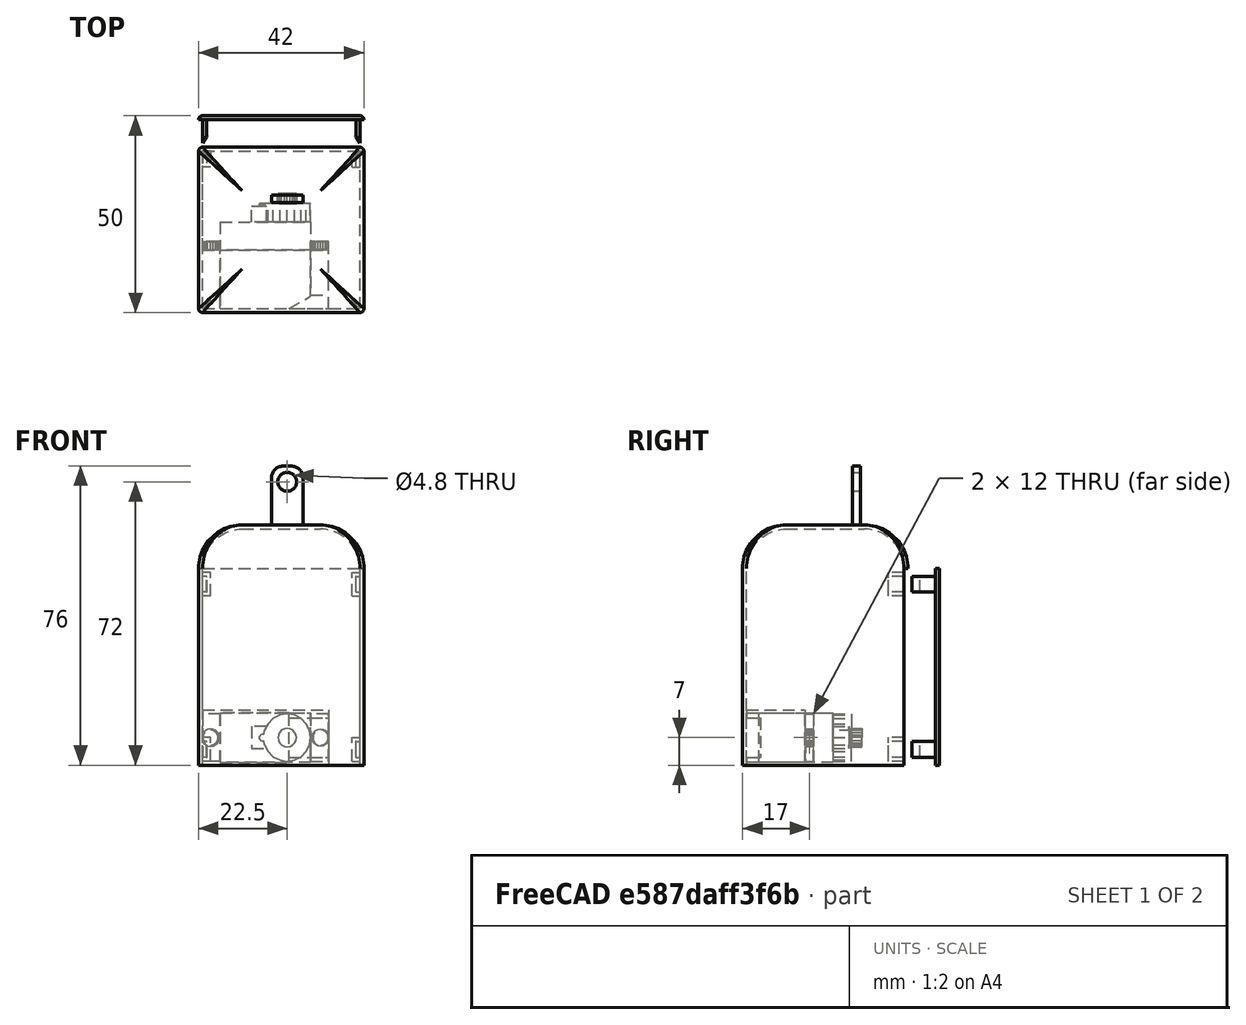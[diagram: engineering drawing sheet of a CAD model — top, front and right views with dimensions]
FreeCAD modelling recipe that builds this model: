
FCSTD DOCUMENT  (FreeCAD 0.21R33771 (Git))
Label: leg draft
License: All rights reserved
LicenseURL: https://en.wikipedia.org/wiki/All_rights_reserved
objects: Part::Box×30, Part::Cut×15, Part::MultiFuse×12, Part::Cylinder×6, Part::Feature×6, Part::Fillet×4, Part::Mirroring×4, App::LinkGroup×2, Part::Thickness×2, Part::MultiCommon×1
note: 80 computed .brp shape members not serialized (recipe doc carries the construction recipe); baked Part::Feature solids carry a one-line shape summary decoded from their .brp

FEATURE [Part::Box] Box  label="leg down"
  AttacherType = Attacher::AttachEngine3D
  Height = 60
  Length = 40
  Placement = pos=(0,0,25) rot=(0,0,1;0rad)
  Width = 40
FEATURE [Part::Box] Box017  label="Cube005"
  AttacherType = Attacher::AttachEngine3D
  Height = 14.9
  Length = 32
  Width = 14
FEATURE [Part::Box] Box018  label="Cube006"
  AttacherType = Attacher::AttachEngine3D
  Height = 3.5
  Length = 10
  Placement = pos=(22,2,0) rot=(0,0,1;0rad)
  Width = 10
FEATURE [Part::Cylinder] Cylinder004  label="Cylindre004"
  Angle = 360
  AttacherType = Attacher::AttachEngine3D
  FirstAngle = 0
  Height = 2.1
  Placement = pos=(2,7,14.9) rot=(0,0,1;0rad)
  Radius = 1.95
  SecondAngle = 0
FEATURE [Part::Cylinder] Cylinder005  label="Cylindre005"
  Angle = 360
  AttacherType = Attacher::AttachEngine3D
  FirstAngle = 0
  Height = 2.1
  Placement = pos=(30,7,14.9) rot=(0,0,1;0rad)
  Radius = 1.95
  SecondAngle = 0
FEATURE [Part::Feature] _g_servo002_solid003  label="9g_servo003"
  Placement = pos=(16,7,11) rot=(0,0,1;0rad)
  shape: bbox 32 x 12.5 x 29.27 mm, 117 faces (baked)
FEATURE [Part::Cut] Cut003
  Base = -> Box017
  Tool = -> _g_servo002_solid003
FEATURE [Part::MultiFuse] Fusion008
  Shapes = -> [Cut003,Cylinder004,Cylinder005]
FEATURE [Part::Cut] Cut004  label="ServoSocket001"
  Base = -> Fusion008
  Placement = pos=(0,0,39) rot=(-1,0,0;1.5708rad)
  Tool = -> Box018
FEATURE [Part::Feature] _g_servo002_solid  label="9g_servo"
  Placement = pos=(16,11,32) rot=(-1,0,0;1.5708rad)
  shape: bbox 32 x 29.27 x 12.5 mm, 117 faces (baked)
FEATURE [Part::Feature] _g_servo_arm_single001
  Placement = pos=(158,31,139) rot=(0,0.707107,-0.707107;3.14159rad)
  shape: bbox 6.653 x 4.702 x 19.83 mm, 2412 faces, 0 solids (baked)
FEATURE [App::LinkGroup] LinkGroup  label="Servo in"
  ElementList = -> [_g_servo002_solid,_g_servo_arm_single001]
  LinkMode = 0
FEATURE [Part::Feature] _g_servo002_solid006  label="9g_servo006"
  Placement = pos=(16,11,32) rot=(-1,0,0;1.5708rad)
  shape: bbox 32 x 29.27 x 12.5 mm, 117 faces (baked)
FEATURE [Part::Feature] _g_servo_arm_single002
  Placement = pos=(158,31,139) rot=(0,0.707107,-0.707107;3.14159rad)
  shape: bbox 6.653 x 4.702 x 19.83 mm, 2412 faces, 0 solids (baked)
FEATURE [App::LinkGroup] LinkGroup001  label="servo up"
  ElementList = -> [_g_servo002_solid006,_g_servo_arm_single002]
  LinkMode = 0
  Placement = pos=(0,-7.62939e-06,65) rot=(0,0,1;0rad)
FEATURE [Part::Box] Box024  label="azeazeaze"
  AttacherType = Attacher::AttachEngine3D
  Height = 15
  Length = 8
  Width = 2
FEATURE [Part::Cylinder] Cylinder010  label="Cylindre010"
  Angle = 360
  AttacherType = Attacher::AttachEngine3D
  FirstAngle = 0
  Height = 10
  Placement = pos=(4,4,11) rot=(1,0,0;1.5708rad)
  Radius = 2.4
  SecondAngle = 0
FEATURE [Part::Cut] Cut
  Base = -> Box024
  Placement = pos=(17.5,26.9,86) rot=(0,0,1;0rad)
  Tool = -> Cylinder010
FEATURE [Part::Fillet] Fillet
  Base = -> Box
  Edges = 4 edges r=10: [Edge2,Edge6,Edge10,Edge12]
FEATURE [Part::Thickness] Thickness
  Faces = -> Fillet [Face4]
  Intersection = true
  Join = 0
  Mode = 0
  SelfIntersection = true
  Value = 1
FEATURE [Part::Fillet] Fillet001
  Base = -> Cut
  Edges = 2 edges r=3: [Edge2,Edge10]
FEATURE [Part::MultiFuse] Fusion
  Shapes = -> [Thickness,Fillet001]
FEATURE [Part::MultiFuse] Fusion011
  Shapes = -> [Fusion,Cut004]
FEATURE [Part::Box] Box025  label="Cube"
  AttacherType = Attacher::AttachEngine3D
  Height = 50
  Length = 42
  Placement = pos=(-1,40,25) rot=(0,0,1;0rad)
  Width = 1
FEATURE [Part::Box] Box026  label="leg down002"
  AttacherType = Attacher::AttachEngine3D
  Height = 60
  Length = 40
  Placement = pos=(0,0,25) rot=(0,0,1;0rad)
  Width = 40
FEATURE [Part::Box] Box027  label="Cube011"
  AttacherType = Attacher::AttachEngine3D
  Height = 14.9
  Length = 32
  Width = 14
FEATURE [Part::Box] Box028  label="Cube012"
  AttacherType = Attacher::AttachEngine3D
  Height = 3.5
  Length = 10
  Placement = pos=(22,2,0) rot=(0,0,1;0rad)
  Width = 10
FEATURE [Part::Box] Box029  label="azeazeaze001"
  AttacherType = Attacher::AttachEngine3D
  Height = 15
  Length = 8
  Width = 2
FEATURE [Part::Cylinder] Cylinder011  label="Cylindre011"
  Angle = 360
  AttacherType = Attacher::AttachEngine3D
  FirstAngle = 0
  Height = 2.1
  Placement = pos=(2,7,14.9) rot=(0,0,1;0rad)
  Radius = 1.95
  SecondAngle = 0
FEATURE [Part::Cylinder] Cylinder012  label="Cylindre012"
  Angle = 360
  AttacherType = Attacher::AttachEngine3D
  FirstAngle = 0
  Height = 2.1
  Placement = pos=(30,7,14.9) rot=(0,0,1;0rad)
  Radius = 1.95
  SecondAngle = 0
FEATURE [Part::Cylinder] Cylinder013  label="Cylindre013"
  Angle = 360
  AttacherType = Attacher::AttachEngine3D
  FirstAngle = 0
  Height = 10
  Placement = pos=(4,4,11) rot=(1,0,0;1.5708rad)
  Radius = 2.4
  SecondAngle = 0
FEATURE [Part::Cut] Cut009
  Base = -> Box029
  Placement = pos=(17.5,26.9,86) rot=(0,0,1;0rad)
  Tool = -> Cylinder013
FEATURE [Part::Fillet] Fillet002
  Base = -> Box026
  Edges = 4 edges r=10: [Edge2,Edge6,Edge10,Edge12]
FEATURE [Part::Fillet] Fillet003
  Base = -> Cut009
  Edges = 2 edges r=3: [Edge2,Edge10]
FEATURE [Part::Thickness] Thickness006
  Faces = -> Fillet002 [Face4]
  Intersection = true
  Join = 0
  Mode = 0
  SelfIntersection = true
  Value = 1
FEATURE [Part::MultiFuse] Fusion012
  Shapes = -> [Thickness006,Fillet003]
FEATURE [Part::Feature] _g_servo002_solid007  label="9g_servo007"
  Placement = pos=(16,7,11) rot=(0,0,1;0rad)
  shape: bbox 32 x 12.5 x 29.27 mm, 117 faces (baked)
FEATURE [Part::Cut] Cut010
  Base = -> Box027
  Tool = -> _g_servo002_solid007
FEATURE [Part::MultiFuse] Fusion013
  Shapes = -> [Cut010,Cylinder011,Cylinder012]
FEATURE [Part::Cut] Cut011  label="ServoSocket004"
  Base = -> Fusion013
  Placement = pos=(0,0,39) rot=(-1,0,0;1.5708rad)
  Tool = -> Box028
FEATURE [Part::MultiFuse] Fusion014
  Shapes = -> [Fusion012,Cut011]
FEATURE [Part::Box] Box030  label="Cube013"
  AttacherType = Attacher::AttachEngine3D
  Height = 50
  Length = 42
  Placement = pos=(-1,40,25) rot=(0,0,1;0rad)
  Width = 1
FEATURE [Part::MultiCommon] Common  label="Leg side"
  Placement = pos=(0,6,0) rot=(0,0,1;0rad)
  Shapes = -> [Fusion014,Box030]
FEATURE [Part::Cut] Cut012  label="Leg body"
  Base = -> Fusion011
  Tool = -> Box025
FEATURE [Part::Box] Box031  label="Cube014"
  AttacherType = Attacher::AttachEngine3D
  Height = 6
  Length = 2
  Width = 4
FEATURE [Part::Box] Box032  label="Cube015"
  AttacherType = Attacher::AttachEngine3D
  Height = 4
  Length = 1
  Placement = pos=(1,0,1) rot=(0,0,1;0rad)
  Width = 4
FEATURE [Part::Box] Box033  label="Cube016"
  AttacherType = Attacher::AttachEngine3D
  Height = 4
  Length = 2
  Placement = pos=(1,0,1) rot=(0,0,-1;0.523599rad)
  Width = 3
FEATURE [Part::Cut] Cut013
  Base = -> Box031
  Placement = pos=(38,36,26) rot=(0,0,1;0rad)
  Tool = -> Box032
FEATURE [Part::Box] Box034  label="Cube017"
  AttacherType = Attacher::AttachEngine3D
  Height = 4
  Length = 1
  Placement = pos=(1,0,1) rot=(0,0,1;0rad)
  Width = 6
FEATURE [Part::Box] Box035  label="Cube018"
  AttacherType = Attacher::AttachEngine3D
  Height = 4
  Length = 1.2
  Placement = pos=(1,0,1) rot=(0,0,1;0rad)
  Width = 2
FEATURE [Part::MultiFuse] Fusion015
  Shapes = -> [Box034,Box035]
FEATURE [Part::Cut] Cut014
  Base = -> Fusion015
  Tool = -> Box033
FEATURE [Part::Mirroring] Part__Mirroring  label="Cut014 (Mirror #1)"
  Base = (0,0,0)
  Normal = (1,0,0)
  Placement = pos=(41,40,26) rot=(0,0,1;0rad)
  Source = -> Cut014
FEATURE [Part::Box] Box036  label="Cube019"
  AttacherType = Attacher::AttachEngine3D
  Height = 6
  Length = 2
  Width = 4
FEATURE [Part::Box] Box037  label="Cube020"
  AttacherType = Attacher::AttachEngine3D
  Height = 4
  Length = 1
  Placement = pos=(1,0,1) rot=(0,0,1;0rad)
  Width = 4
FEATURE [Part::Cut] Cut015
  Base = -> Box036
  Placement = pos=(38,36,68) rot=(0,0,1;0rad)
  Tool = -> Box037
FEATURE [Part::Box] Box038  label="Cube021"
  AttacherType = Attacher::AttachEngine3D
  Height = 4
  Length = 2
  Placement = pos=(1,0,1) rot=(0,0,-1;0.523599rad)
  Width = 3
FEATURE [Part::Box] Box039  label="Cube022"
  AttacherType = Attacher::AttachEngine3D
  Height = 4
  Length = 1
  Placement = pos=(1,0,1) rot=(0,0,1;0rad)
  Width = 6
FEATURE [Part::Box] Box040  label="Cube023"
  AttacherType = Attacher::AttachEngine3D
  Height = 4
  Length = 1.2
  Placement = pos=(1,0,1) rot=(0,0,1;0rad)
  Width = 2
FEATURE [Part::MultiFuse] Fusion016
  Shapes = -> [Box039,Box040]
FEATURE [Part::Cut] Cut016
  Base = -> Fusion016
  Tool = -> Box038
FEATURE [Part::Mirroring] Part__Mirroring001  label="Cut014 (Mirror #1)001"
  Base = (0,0,0)
  Normal = (1,0,0)
  Placement = pos=(41,40,68) rot=(0,0,1;0rad)
  Source = -> Cut016
FEATURE [Part::Box] Box043  label="Cube026"
  AttacherType = Attacher::AttachEngine3D
  Height = 6
  Length = 2
  Width = 4
FEATURE [Part::Box] Box044  label="Cube027"
  AttacherType = Attacher::AttachEngine3D
  Height = 4
  Length = 1
  Placement = pos=(1,0,1) rot=(0,0,1;0rad)
  Width = 4
FEATURE [Part::Cut] Cut018
  Base = -> Box043
  Placement = pos=(2,40,26) rot=(0,0,1;3.14159rad)
  Tool = -> Box044
FEATURE [Part::Box] Box045  label="Cube028"
  AttacherType = Attacher::AttachEngine3D
  Height = 6
  Length = 2
  Width = 4
FEATURE [Part::Box] Box046  label="Cube029"
  AttacherType = Attacher::AttachEngine3D
  Height = 4
  Length = 1
  Placement = pos=(1,0,1) rot=(0,0,1;0rad)
  Width = 4
FEATURE [Part::Cut] Cut019
  Base = -> Box045
  Placement = pos=(2,40,68) rot=(0,0,1;3.14159rad)
  Tool = -> Box046
FEATURE [Part::Box] Box047  label="Cube030"
  AttacherType = Attacher::AttachEngine3D
  Height = 4
  Length = 2
  Placement = pos=(1,0,1) rot=(0,0,-1;0.523599rad)
  Width = 3
FEATURE [Part::Box] Box048  label="Cube031"
  AttacherType = Attacher::AttachEngine3D
  Height = 4
  Length = 1
  Placement = pos=(1,0,1) rot=(0,0,1;0rad)
  Width = 6
FEATURE [Part::Box] Box049  label="Cube032"
  AttacherType = Attacher::AttachEngine3D
  Height = 4
  Length = 1.2
  Placement = pos=(1,0,1) rot=(0,0,1;0rad)
  Width = 2
FEATURE [Part::MultiFuse] Fusion017
  Shapes = -> [Box048,Box049]
FEATURE [Part::Cut] Cut020
  Base = -> Fusion017
  Tool = -> Box047
FEATURE [Part::Mirroring] Part__Mirroring002  label="Cut014 (Mirror #1)002"
  Base = (0,0,0)
  Normal = (1,0,0)
  Placement = pos=(-1,40,32) rot=(0,1,0;3.14159rad)
  Source = -> Cut020
FEATURE [Part::Box] Box050  label="Cube033"
  AttacherType = Attacher::AttachEngine3D
  Height = 4
  Length = 2
  Placement = pos=(1,0,1) rot=(0,0,-1;0.523599rad)
  Width = 3
FEATURE [Part::Box] Box051  label="Cube034"
  AttacherType = Attacher::AttachEngine3D
  Height = 4
  Length = 1
  Placement = pos=(1,0,1) rot=(0,0,1;0rad)
  Width = 6
FEATURE [Part::Box] Box052  label="Cube035"
  AttacherType = Attacher::AttachEngine3D
  Height = 4
  Length = 1.2
  Placement = pos=(1,0,1) rot=(0,0,1;0rad)
  Width = 2
FEATURE [Part::MultiFuse] Fusion018
  Shapes = -> [Box051,Box052]
FEATURE [Part::Cut] Cut021
  Base = -> Fusion018
  Tool = -> Box050
FEATURE [Part::Mirroring] Part__Mirroring003  label="Cut014 (Mirror #1)003"
  Base = (0,0,0)
  Normal = (1,0,0)
  Placement = pos=(-1,40,74) rot=(0,1,0;3.14159rad)
  Source = -> Cut021
FEATURE [Part::MultiFuse] Fusion019  label="Leg side001"
  Placement = pos=(0,2,0) rot=(0,0,1;0rad)
  Shapes = -> [Common,Part__Mirroring,Part__Mirroring001,Part__Mirroring002,Part__Mirroring003]
FEATURE [Part::MultiFuse] Fusion020  label="leg body"
  Shapes = -> [Cut012,Cut013,Cut015,Cut018,Cut019]
